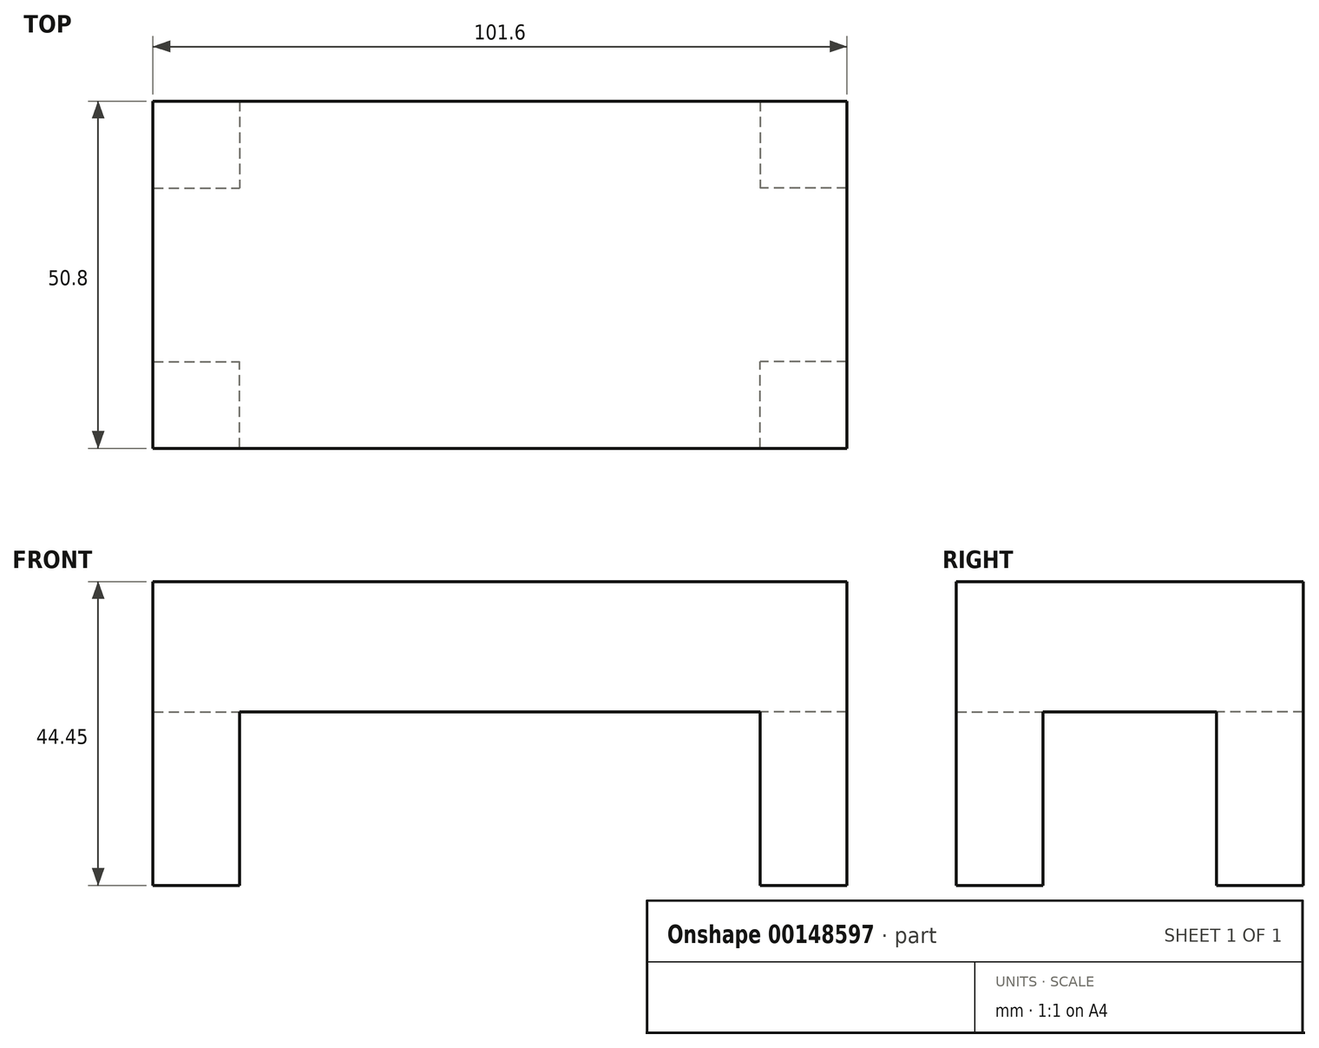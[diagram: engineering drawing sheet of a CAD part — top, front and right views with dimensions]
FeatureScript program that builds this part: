
annotation { "Feature Type Name" : "Feature", "Feature Type Description" : "" }
export const myFeature = defineFeature(function(context is Context, id is Id, definition is map)
    precondition{}
    {
        {
            var Q0;
            Q0=qCreatedBy(makeId("Top.planeOp"),FACE);
            var sketch = newSketch(context, id + "F0", { "sketchPlane" : qUnion([Q0])});
            skLineSegment(sketch, "E0.bottom", {"start": v(-39.8, 13.8) * mm, "end": v(61.8, 13.8) * mm});
            skLineSegment(sketch, "E0.top", {"start": v(-39.8, -37) * mm, "end": v(61.8, -37) * mm});
            skLineSegment(sketch, "E0.left", {"start": v(-39.8, 13.8) * mm, "end": v(-39.8, -37) * mm});
            skLineSegment(sketch, "E0.right", {"start": v(61.8, 13.8) * mm, "end": v(61.8, -37) * mm});
            skSolve(sketch);
        }
        {
            var Q0;
            Q0=makeQuery(id+"F0.imprint","IMPRINT",FACE,{"disambiguationData":[TD([[makeQuery(id+"F0.imprint","IMPRINT",EDGE,{"derivedFrom":sQuery(id+"F0.wireOp",EDGE,"E0.bottom")}),-1.0]])]});
            extrude(context, id + "F1", {"entities" : qUnion([Q0]), "depth" : 19.05 * mm});
        }
        {
            var Q0;
            Q0=makeQuery(id+"F1.opExtrude","CAP_FACE",FACE,{"disambiguationData":[OSD([sQuery(id+"F0.wireOp",EDGE,"E0.bottom"),sQuery(id+"F0.wireOp",EDGE,"E0.top"),sQuery(id+"F0.wireOp",EDGE,"E0.left"),sQuery(id+"F0.wireOp",EDGE,"E0.right")])],"isStart":true});
            var sketch = newSketch(context, id + "F2", { "sketchPlane" : qUnion([Q0])});
            skLineSegment(sketch, "E1.bottom", {"start": v(-39.8, 37) * mm, "end": v(-27.1, 37) * mm});
            skLineSegment(sketch, "E1.top", {"start": v(-39.8, 24.3) * mm, "end": v(-27.1, 24.3) * mm});
            skLineSegment(sketch, "E1.left", {"start": v(-39.8, 37) * mm, "end": v(-39.8, 24.3) * mm});
            skLineSegment(sketch, "E1.right", {"start": v(-27.1, 37) * mm, "end": v(-27.1, 24.3) * mm});
            skLineSegment(sketch, "E2.bottom", {"start": v(61.8, 37) * mm, "end": v(49.1, 37) * mm});
            skLineSegment(sketch, "E2.top", {"start": v(61.8, 24.3) * mm, "end": v(49.1, 24.3) * mm});
            skLineSegment(sketch, "E2.left", {"start": v(61.8, 37) * mm, "end": v(61.8, 24.3) * mm});
            skLineSegment(sketch, "E2.right", {"start": v(49.1, 37) * mm, "end": v(49.1, 24.3) * mm});
            skLineSegment(sketch, "E3.bottom", {"start": v(61.8, -13.8) * mm, "end": v(49.1, -13.8) * mm});
            skLineSegment(sketch, "E3.top", {"start": v(61.8, -1.1) * mm, "end": v(49.1, -1.1) * mm});
            skLineSegment(sketch, "E3.left", {"start": v(61.8, -13.8) * mm, "end": v(61.8, -1.1) * mm});
            skLineSegment(sketch, "E3.right", {"start": v(49.1, -13.8) * mm, "end": v(49.1, -1.1) * mm});
            skLineSegment(sketch, "E4.bottom", {"start": v(-39.8, -13.8) * mm, "end": v(-27.1, -13.8) * mm});
            skLineSegment(sketch, "E4.top", {"start": v(-39.8, -1.1) * mm, "end": v(-27.1, -1.1) * mm});
            skLineSegment(sketch, "E4.left", {"start": v(-39.8, -13.8) * mm, "end": v(-39.8, -1.1) * mm});
            skLineSegment(sketch, "E4.right", {"start": v(-27.1, -13.8) * mm, "end": v(-27.1, -1.1) * mm});
            skSolve(sketch);
        }
        {
            var Q0;
            Q0=makeQuery(id+"F2.imprint","IMPRINT",FACE,{"disambiguationData":[TD([[makeQuery(id+"F2.imprint","IMPRINT",EDGE,{"derivedFrom":sQuery(id+"F2.wireOp",EDGE,"E2.bottom")}),-1.0]])]});
            var Q1;
            Q1=makeQuery(id+"F2.imprint","IMPRINT",FACE,{"disambiguationData":[TD([[makeQuery(id+"F2.imprint","IMPRINT",EDGE,{"derivedFrom":sQuery(id+"F2.wireOp",EDGE,"E3.bottom")}),1.0]])]});
            var Q2;
            Q2=makeQuery(id+"F2.imprint","IMPRINT",FACE,{"disambiguationData":[TD([[makeQuery(id+"F2.imprint","IMPRINT",EDGE,{"derivedFrom":sQuery(id+"F2.wireOp",EDGE,"E4.bottom")}),1.0]])]});
            var Q3;
            Q3=makeQuery(id+"F2.imprint","IMPRINT",FACE,{"disambiguationData":[TD([[makeQuery(id+"F2.imprint","IMPRINT",EDGE,{"derivedFrom":sQuery(id+"F2.wireOp",EDGE,"E1.bottom")}),-1.0]])]});
            extrude(context, id + "F3", {"entities" : qUnion([Q0, Q1, Q2, Q3]), "operationType" : NewBodyOperationType.ADD, "depth" : 25.4 * mm});
        }
    });
